# Revit family: Zumtobel MIREL-L LAY LED M625L
name_source: partatom
category: Leuchten
units: mm (PartAtom-declared; Revit-internal decimal feet)

## family parameters
Basisbauteil = Fläche
Beim Laden mit Abzugskörper schneiden = Nein
Bemaßung runder Anschluss = Durchmesser verwenden
Beschriftungsausrichtung beibehalten = Nein
Gemeinsam genutzt = Nein
Lichtquelle = Ja
OmniClass-Nummer = 23.80.70.11
OmniClass-Titel = Luminaries for Internal Lighting
Raumberechnungspunkt = Nein
Teiletyp = Normal

## types (2) — shared parameters
Baugruppenkennzeichen = D5020200
Beschreibung = LED recessed luminaire
Emissionsform beim Rendern sichtbar = Ja
Farbfilter = 16777215
Farbtemperaturverschiebung bei Dämpfen der Lampe = <Keine Auswahl>
Height = 38 mm  [stored 0.124672 ft]
Hersteller = Zumtobel Lighting
Lampe = LED
Length = 1248 mm  [stored 4.09449 ft]
Neigungswinkel = 90.00°
URL = http://www.zumtobel.com
Voltage = 230 V
Von Breite des Rechtecks ausssenden = 1248 mm  [stored 4.09449 ft]
Von Länge des Rechtecks aussenden = 310 mm  [stored 1.01706 ft]
Width = 310 mm  [stored 1.01706 ft]
zero-valued in all types: Vorgabe-Ansicht

## per-type parameters (varying)
| type | Datei für fotometrisches Netz | Modell | Scheinlast |
| MIREL-L LAY LED3800-840 M600L EVG KA | 42182363_(STD).IES | 42182363 | 37 VA |
| MIREL-L LAY LED3800-840 M600L LDO KA | 42952571_(STD).IES | 42952571 | 28 VA |

note: [stored X ft] marks values corroborated as IEEE doubles in the binary element streams (Revit-internal decimal feet)

## geometry (parser evidence)
native form markers: Sweep x2
no freeform markers — native parametric forms only
